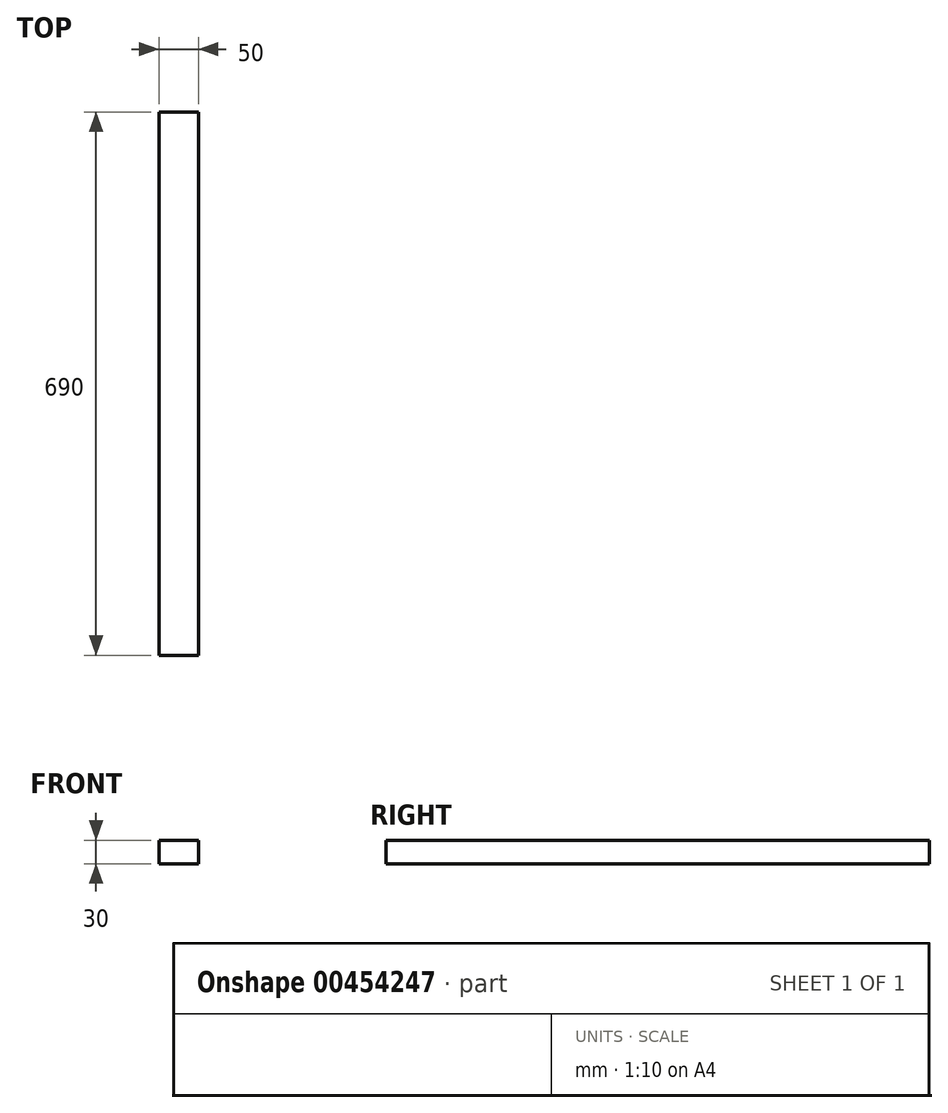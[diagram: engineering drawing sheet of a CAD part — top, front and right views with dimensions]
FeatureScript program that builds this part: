
annotation { "Feature Type Name" : "Feature", "Feature Type Description" : "" }
export const myFeature = defineFeature(function(context is Context, id is Id, definition is map)
    precondition{}
    {
        {
            var Q0;
            Q0=qCreatedBy(makeId("Front.planeOp"),FACE);
            var sketch = newSketch(context, id + "F0", { "sketchPlane" : qUnion([Q0])});
            skLineSegment(sketch, "E0.bottom", {"start": v(-23.35, 15) * mm, "end": v(26.65, 15) * mm});
            skLineSegment(sketch, "E0.top", {"start": v(-23.35, -15) * mm, "end": v(26.65, -15) * mm});
            skLineSegment(sketch, "E0.left", {"start": v(-23.35, 15) * mm, "end": v(-23.35, -15) * mm});
            skLineSegment(sketch, "E0.right", {"start": v(26.65, 15) * mm, "end": v(26.65, -15) * mm});
            skPoint(sketch, "E0.middle", {"position": v(1.65, 0) * mm});
            skSolve(sketch);
        }
        {
            var Q0;
            Q0=makeQuery(id+"F0.imprint","IMPRINT",FACE,{"disambiguationData":[TD([[makeQuery(id+"F0.imprint","IMPRINT",EDGE,{"derivedFrom":sQuery(id+"F0.wireOp",EDGE,"E0.bottom")}),-1.0]])]});
            extrude(context, id + "F1", {"entities" : qUnion([Q0]), "depth" : 690 * mm});
        }
    });
